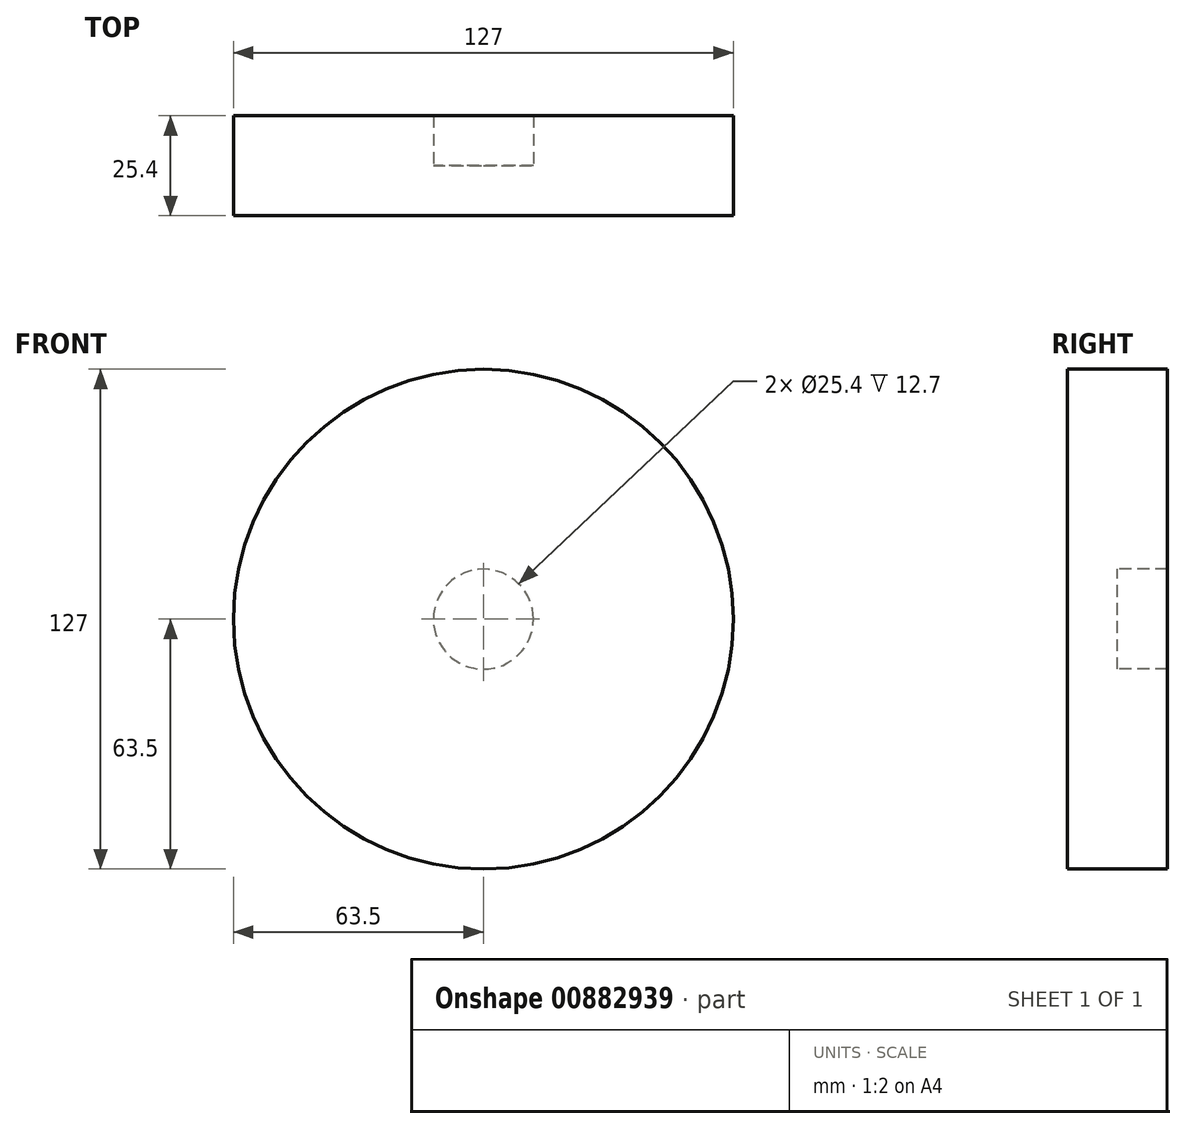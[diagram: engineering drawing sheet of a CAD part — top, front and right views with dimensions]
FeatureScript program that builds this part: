
annotation { "Feature Type Name" : "Feature", "Feature Type Description" : "" }
export const myFeature = defineFeature(function(context is Context, id is Id, definition is map)
    precondition{}
    {
        {
            var Q0;
            Q0=qCreatedBy(makeId("Front.planeOp"),FACE);
            var sketch = newSketch(context, id + "F0", { "sketchPlane" : qUnion([Q0])});
            skCircle(sketch, "E0", {"center": v(0, 0) * mm, "radius": 63.5 * mm});
            skSolve(sketch);
        }
        {
            var Q0;
            Q0=makeQuery(id+"F0.imprint","IMPRINT",FACE,{"disambiguationData":[TD([[makeQuery(id+"F0.imprint","IMPRINT",EDGE,{"derivedFrom":sQuery(id+"F0.wireOp",EDGE,"E0")}),1.0]])]});
            extrude(context, id + "F1", {"entities" : qUnion([Q0]), "depth" : 12.7 * mm, "offsetDistance" : 25.4 * mm, "hasSecondDirection" : true, "secondDirectionOppositeDirection" : true, "secondDirectionDepth" : 12.7 * mm});
        }
        {
            var Q0;
            Q0=qCreatedBy(makeId("Front.planeOp"),FACE);
            var sketch = newSketch(context, id + "F2", { "sketchPlane" : qUnion([Q0])});
            skCircle(sketch, "E1", {"center": v(0, 0) * mm, "radius": 12.7 * mm});
            skSolve(sketch);
        }
        {
            var Q0;
            Q0 = qSketchRegion(id + "F2", true);
            extrude(context, id + "F3", {"entities" : qUnion([Q0]), "operationType" : NewBodyOperationType.REMOVE, "oppositeDirection" : true, "depth" : 25.4 * mm, "offsetDistance" : 25.4 * mm});
        }
    });
